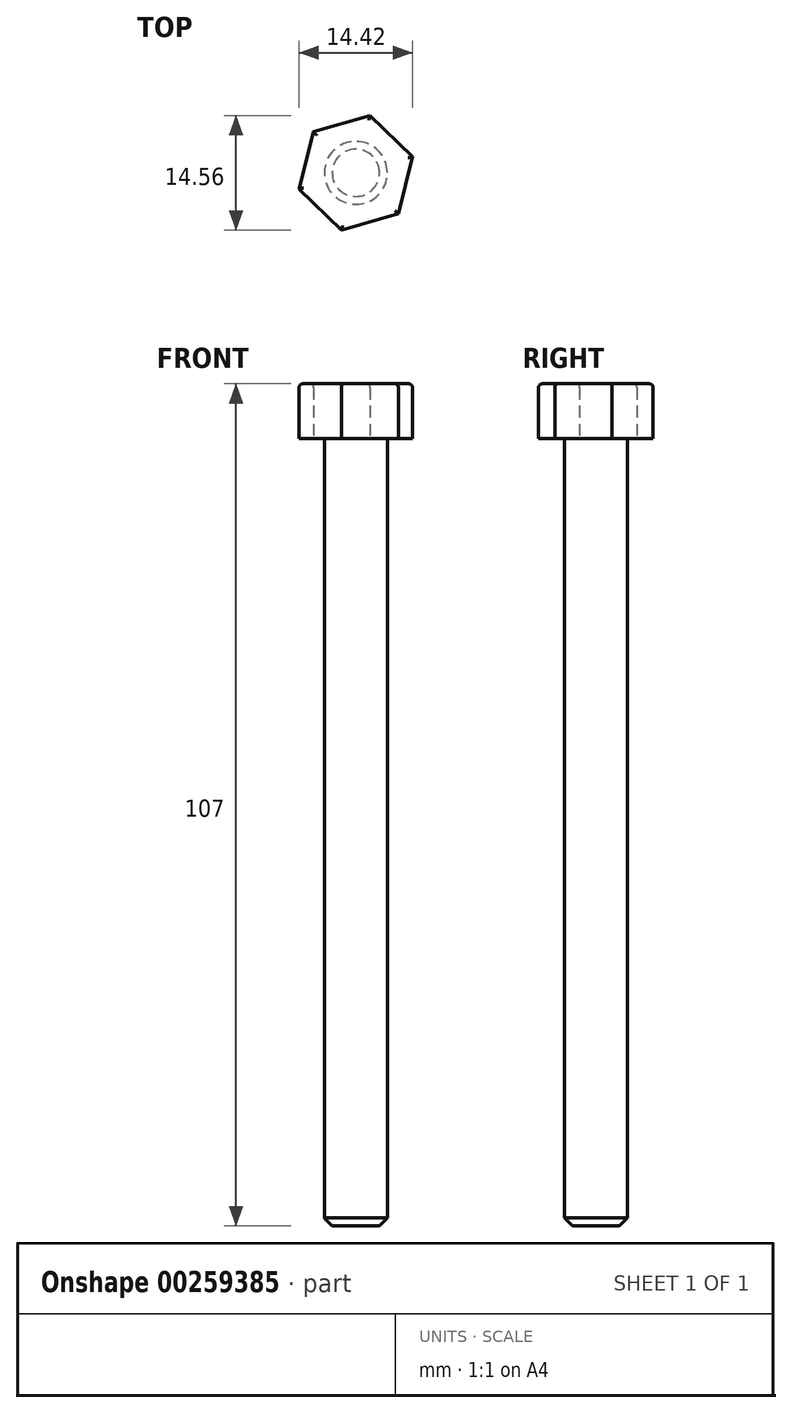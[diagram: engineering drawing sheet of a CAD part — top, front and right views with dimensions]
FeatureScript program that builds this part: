
annotation { "Feature Type Name" : "Feature", "Feature Type Description" : "" }
export const myFeature = defineFeature(function(context is Context, id is Id, definition is map)
    precondition{}
    {
        {
            var Q0;
            Q0=qCreatedBy(makeId("Top.planeOp"),FACE);
            var sketch = newSketch(context, id + "F0", { "sketchPlane" : qUnion([Q0])});
            skCircle(sketch, "E0.cCircle", {"center": v(0, 0) * mm, "radius": 6.5 * mm, "construction": true});
            skLineSegment(sketch, "E0.0", {"start": v(-5.4, 5.2) * mm, "end": v(1.8, 7.28) * mm});
            skLineSegment(sketch, "E0.1", {"start": v(1.8, 7.28) * mm, "end": v(7.21, 2.08) * mm});
            skLineSegment(sketch, "E0.2", {"start": v(7.21, 2.08) * mm, "end": v(5.4, -5.2) * mm});
            skLineSegment(sketch, "E0.3", {"start": v(5.4, -5.2) * mm, "end": v(-1.8, -7.28) * mm});
            skLineSegment(sketch, "E0.4", {"start": v(-1.8, -7.28) * mm, "end": v(-7.21, -2.08) * mm});
            skLineSegment(sketch, "E0.5", {"start": v(-7.21, -2.08) * mm, "end": v(-5.4, 5.2) * mm});
            skPoint(sketch, "E0.0.midPoint", {"position": v(-1.8, 6.25) * mm});
            skSolve(sketch);
        }
        {
            var Q0;
            Q0 = qSketchRegion(id + "F0", true);
            extrude(context, id + "F1", {"entities" : qUnion([Q0]), "depth" : 7 * mm});
        }
        {
            var Q0;
            Q0=makeQuery(id+"F1.opExtrude","CAP_EDGE",EDGE,{"disambiguationData":[OSD([sQuery(id+"F0.wireOp",EDGE,"E0.4")])],"isStart":false});
            var Q1;
            Q1=makeQuery(id+"F1.opExtrude","CAP_EDGE",EDGE,{"disambiguationData":[OSD([sQuery(id+"F0.wireOp",EDGE,"E0.3")])],"isStart":false});
            var Q2;
            Q2=makeQuery(id+"F1.opExtrude","CAP_FACE",FACE,{"disambiguationData":[OSD([sQuery(id+"F0.wireOp",EDGE,"E0.0"),sQuery(id+"F0.wireOp",EDGE,"E0.1"),sQuery(id+"F0.wireOp",EDGE,"E0.2"),sQuery(id+"F0.wireOp",EDGE,"E0.3"),sQuery(id+"F0.wireOp",EDGE,"E0.4"),sQuery(id+"F0.wireOp",EDGE,"E0.5")])],"isStart":false});
            fillet(context, id + "F2", {"entities" : qUnion([Q0, Q1, Q2]), "radius" : 0.5 * mm, "tangentPropagation" : true, "allowEdgeOverflow" : false});
        }
        {
            var Q0;
            Q0=makeQuery(id+"F1.opExtrude","CAP_FACE",FACE,{"disambiguationData":[OSD([sQuery(id+"F0.wireOp",EDGE,"E0.0"),sQuery(id+"F0.wireOp",EDGE,"E0.1"),sQuery(id+"F0.wireOp",EDGE,"E0.2"),sQuery(id+"F0.wireOp",EDGE,"E0.3"),sQuery(id+"F0.wireOp",EDGE,"E0.4"),sQuery(id+"F0.wireOp",EDGE,"E0.5")])],"isStart":true});
            var sketch = newSketch(context, id + "F3", { "sketchPlane" : qUnion([Q0])});
            skCircle(sketch, "E1", {"center": v(0, 0) * mm, "radius": 4 * mm});
            skSolve(sketch);
        }
        {
            var Q0;
            Q0 = qSketchRegion(id + "F3", true);
            extrude(context, id + "F4", {"entities" : qUnion([Q0]), "operationType" : NewBodyOperationType.ADD, "depth" : 100 * mm});
        }
        {
            var Q0;
            Q0=makeQuery(id+"F4.opExtrude","CAP_EDGE",EDGE,{"disambiguationData":[OSD([sQuery(id+"F3.wireOp",EDGE,"E1")])],"isStart":false});
            chamfer(context, id + "F5", {"entities" : qUnion([Q0]), "width" : 1 * mm, "tangentPropagation" : true});
        }
    });
